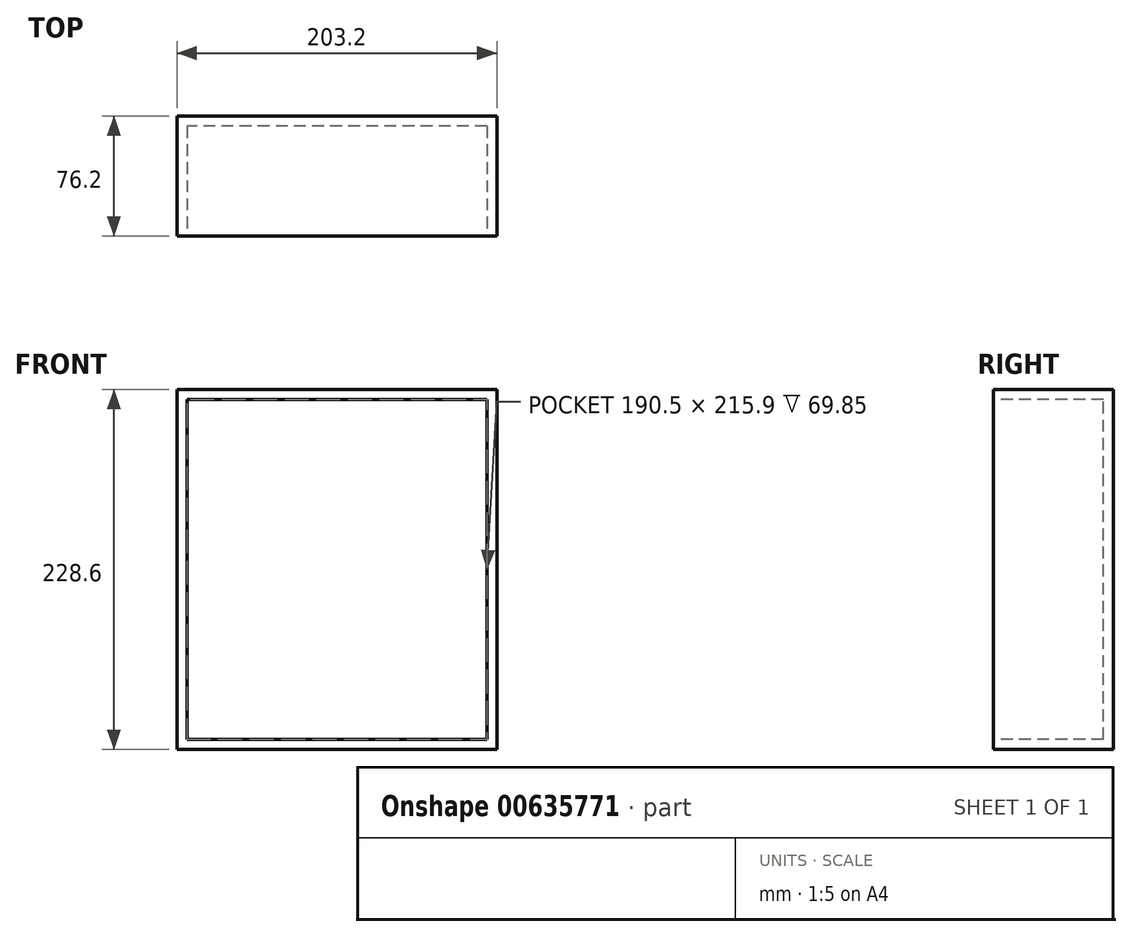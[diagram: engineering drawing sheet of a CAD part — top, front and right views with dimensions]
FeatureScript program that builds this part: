
annotation { "Feature Type Name" : "Feature", "Feature Type Description" : "" }
export const myFeature = defineFeature(function(context is Context, id is Id, definition is map)
    precondition{}
    {
        {
            var Q0;
            Q0=qCreatedBy(makeId("Front.planeOp"),FACE);
            var sketch = newSketch(context, id + "F0", { "sketchPlane" : qUnion([Q0])});
            skLineSegment(sketch, "E0.bottom", {"start": v(101.6, -114.3) * mm, "end": v(-101.6, -114.3) * mm});
            skLineSegment(sketch, "E0.top", {"start": v(101.6, 114.3) * mm, "end": v(-101.6, 114.3) * mm});
            skLineSegment(sketch, "E0.left", {"start": v(101.6, -114.3) * mm, "end": v(101.6, 114.3) * mm});
            skLineSegment(sketch, "E0.right", {"start": v(-101.6, -114.3) * mm, "end": v(-101.6, 114.3) * mm});
            skPoint(sketch, "E0.middle", {"position": v(0, 0) * mm});
            skLineSegment(sketch, "E1.bottom", {"start": v(95.25, -107.95) * mm, "end": v(-95.25, -107.95) * mm});
            skLineSegment(sketch, "E1.top", {"start": v(95.25, 107.95) * mm, "end": v(-95.25, 107.95) * mm});
            skLineSegment(sketch, "E1.left", {"start": v(95.25, -107.95) * mm, "end": v(95.25, 107.95) * mm});
            skLineSegment(sketch, "E1.right", {"start": v(-95.25, -107.95) * mm, "end": v(-95.25, 107.95) * mm});
            skSolve(sketch);
        }
        {
            var Q0;
            Q0=makeQuery(id+"F0.imprint","IMPRINT",FACE,{"disambiguationData":[TD([[makeQuery(id+"F0.imprint","IMPRINT",EDGE,{"derivedFrom":sQuery(id+"F0.wireOp",EDGE,"E0.bottom")}),-1.0]])]});
            extrude(context, id + "F1", {"entities" : qUnion([Q0]), "oppositeDirection" : true, "depth" : 76.2 * mm, "offsetDistance" : 25.4 * mm});
        }
        {
            var Q0;
            Q0=makeQuery(id+"F0.imprint","IMPRINT",FACE,{"disambiguationData":[TD([[makeQuery(id+"F0.imprint","IMPRINT",EDGE,{"derivedFrom":sQuery(id+"F0.wireOp",EDGE,"E1.bottom")}),-1.0]])]});
            extrude(context, id + "F2", {"entities" : qUnion([Q0]), "operationType" : NewBodyOperationType.ADD, "oppositeDirection" : true, "depth" : 76.2 * mm, "offsetDistance" : 25.4 * mm});
        }
        {
            var Q0;
            Q0=makeQuery(id+"F0.imprint","IMPRINT",FACE,{"disambiguationData":[TD([[makeQuery(id+"F0.imprint","IMPRINT",EDGE,{"derivedFrom":sQuery(id+"F0.wireOp",EDGE,"E1.bottom")}),-1.0]])]});
            extrude(context, id + "F3", {"entities" : qUnion([Q0]), "operationType" : NewBodyOperationType.REMOVE, "oppositeDirection" : true, "depth" : 69.85 * mm, "offsetDistance" : 25.4 * mm});
        }
    });
